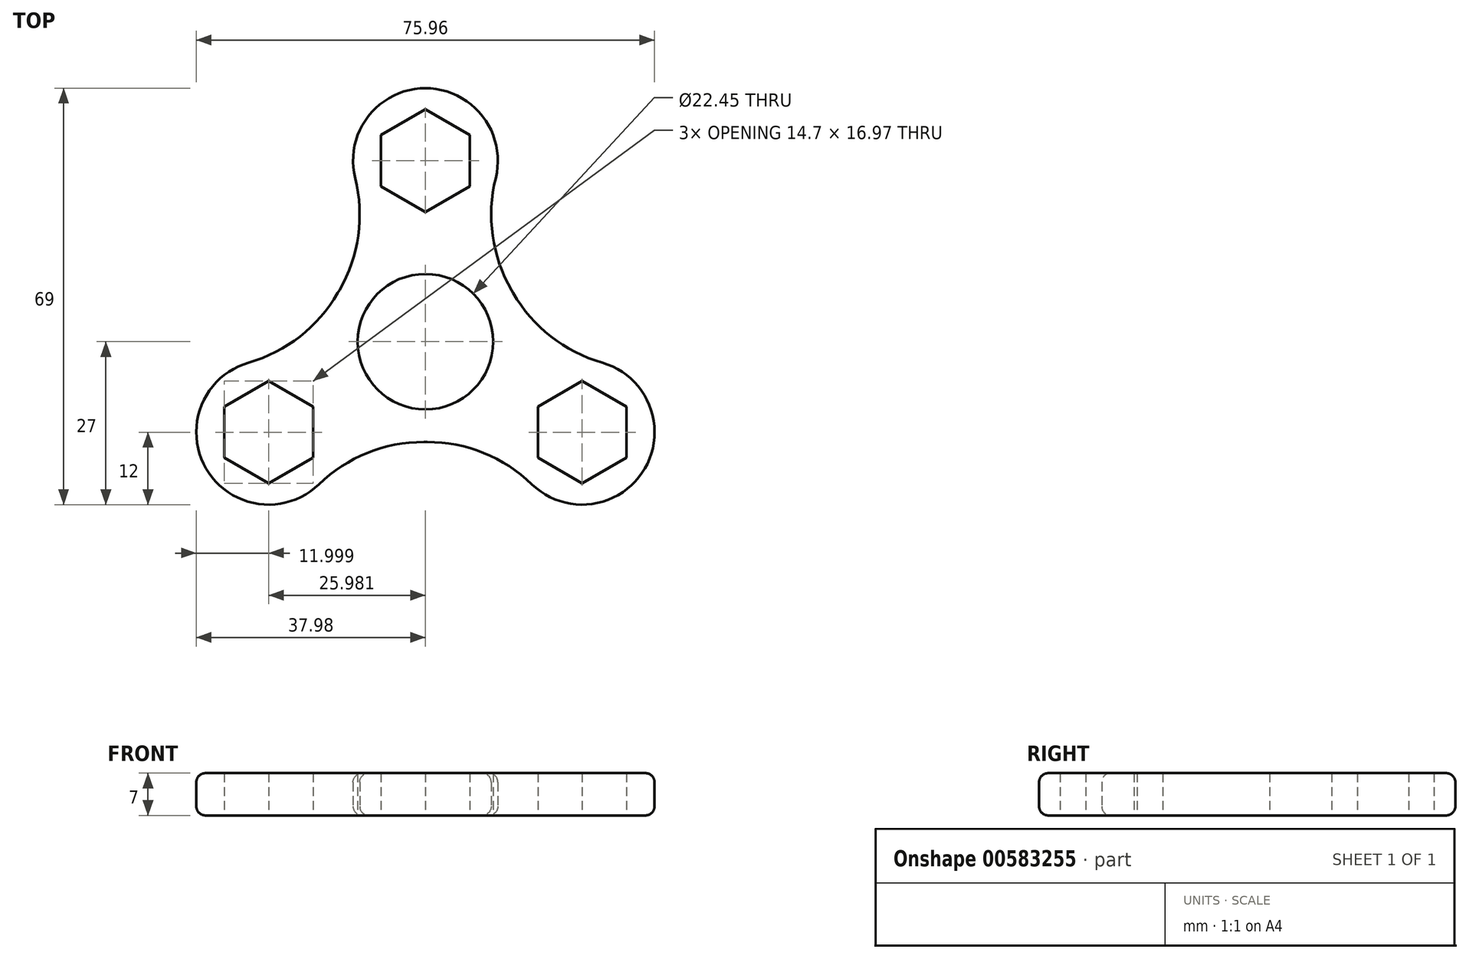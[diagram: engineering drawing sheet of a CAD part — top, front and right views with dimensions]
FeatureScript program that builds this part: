
annotation { "Feature Type Name" : "Feature", "Feature Type Description" : "" }
export const myFeature = defineFeature(function(context is Context, id is Id, definition is map)
    precondition{}
    {
        {
            var Q0;
            Q0=qCreatedBy(makeId("Top.planeOp"),FACE);
            var sketch = newSketch(context, id + "F0", { "sketchPlane" : qUnion([Q0])});
            skCircle(sketch, "E0", {"center": v(0, 0) * mm, "radius": 11.23 * mm});
            skCircle(sketch, "E1.cCircle", {"center": v(0, 30) * mm, "radius": 7.35 * mm, "construction": true});
            skLineSegment(sketch, "E1.0", {"start": v(7.35, 34.24) * mm, "end": v(7.35, 25.76) * mm});
            skLineSegment(sketch, "E1.1", {"start": v(7.35, 25.76) * mm, "end": v(0, 21.51) * mm});
            skLineSegment(sketch, "E1.2", {"start": v(0, 21.51) * mm, "end": v(-7.35, 25.76) * mm});
            skLineSegment(sketch, "E1.3", {"start": v(-7.35, 25.76) * mm, "end": v(-7.35, 34.24) * mm});
            skLineSegment(sketch, "E1.4", {"start": v(-7.35, 34.24) * mm, "end": v(0, 38.49) * mm});
            skLineSegment(sketch, "E1.5", {"start": v(0, 38.49) * mm, "end": v(7.35, 34.24) * mm});
            skPoint(sketch, "E1.0.midPoint", {"position": v(7.35, 30) * mm});
            skPoint(sketch, "E2.1.0", {"position": v(-29.66, -8.63) * mm});
            skLineSegment(sketch, "E2.1.1", {"start": v(-33.33, -19.24) * mm, "end": v(-33.33, -10.76) * mm});
            skLineSegment(sketch, "E2.1.2", {"start": v(-25.98, -23.49) * mm, "end": v(-33.33, -19.24) * mm});
            skLineSegment(sketch, "E2.1.3", {"start": v(-18.63, -19.24) * mm, "end": v(-25.98, -23.49) * mm});
            skLineSegment(sketch, "E2.1.4", {"start": v(-18.63, -10.76) * mm, "end": v(-18.63, -19.24) * mm});
            skLineSegment(sketch, "E2.1.5", {"start": v(-25.98, -6.51) * mm, "end": v(-18.63, -10.76) * mm});
            skLineSegment(sketch, "E2.1.6", {"start": v(-33.33, -10.76) * mm, "end": v(-25.98, -6.51) * mm});
            skCircle(sketch, "E2.1.7", {"center": v(-25.98, -15) * mm, "radius": 7.35 * mm, "construction": true});
            skPoint(sketch, "E2.2.0", {"position": v(22.3, -21.37) * mm});
            skLineSegment(sketch, "E2.2.1", {"start": v(33.33, -19.24) * mm, "end": v(25.98, -23.49) * mm});
            skLineSegment(sketch, "E2.2.2", {"start": v(33.33, -10.76) * mm, "end": v(33.33, -19.24) * mm});
            skLineSegment(sketch, "E2.2.3", {"start": v(25.98, -6.51) * mm, "end": v(33.33, -10.76) * mm});
            skLineSegment(sketch, "E2.2.4", {"start": v(18.63, -10.76) * mm, "end": v(25.98, -6.51) * mm});
            skLineSegment(sketch, "E2.2.5", {"start": v(18.63, -19.24) * mm, "end": v(18.63, -10.76) * mm});
            skLineSegment(sketch, "E2.2.6", {"start": v(25.98, -23.49) * mm, "end": v(18.63, -19.24) * mm});
            skCircle(sketch, "E2.2.7", {"center": v(25.98, -15) * mm, "radius": 7.35 * mm, "construction": true});
            skArc(sketch, "E3.0", {"start": v(-8.85, -13.6) * mm, "mid": v(0, -16.23) * mm, "end": v(8.85, -13.6) * mm});
            skArc(sketch, "E4", {"start": v(-21.44, -3.9) * mm, "mid": v(-36.37, -21) * mm, "end": v(-14.1, -16.62) * mm});
            skArc(sketch, "E5", {"start": v(7.35, 20.51) * mm, "mid": v(0, 42) * mm, "end": v(-7.35, 20.51) * mm});
            skArc(sketch, "E6", {"start": v(14.1, -16.62) * mm, "mid": v(36.37, -21) * mm, "end": v(21.44, -3.9) * mm});
            skLineSegment(sketch, "E7", {"start": v(-14.1, -16.62) * mm, "end": v(-8.85, -13.6) * mm});
            skLineSegment(sketch, "E8", {"start": v(-21.44, -3.9) * mm, "end": v(-16.2, -0.87) * mm});
            skLineSegment(sketch, "E9.1.0", {"start": v(14.1, -16.62) * mm, "end": v(8.85, -13.6) * mm});
            skLineSegment(sketch, "E9.1.1", {"start": v(21.44, -3.9) * mm, "end": v(16.2, -0.87) * mm});
            skLineSegment(sketch, "E9.2.0", {"start": v(7.35, 20.51) * mm, "end": v(7.35, 14.46) * mm});
            skLineSegment(sketch, "E9.2.1", {"start": v(-7.35, 20.51) * mm, "end": v(-7.35, 14.46) * mm});
            skArc(sketch, "E10.trimOffspring", {"start": v(16.2, -0.87) * mm, "mid": v(14.05, 8.11) * mm, "end": v(7.35, 14.46) * mm});
            skArc(sketch, "E11.trimOffspring", {"start": v(-7.35, 14.46) * mm, "mid": v(-14.05, 8.11) * mm, "end": v(-16.2, -0.87) * mm});
            skLineSegment(sketch, "E12", {"start": v(-7.35, 20.51) * mm, "end": v(-21.44, -3.9) * mm});
            skLineSegment(sketch, "E13", {"start": v(7.35, 20.51) * mm, "end": v(21.44, -3.9) * mm});
            skLineSegment(sketch, "E14", {"start": v(14.1, -16.62) * mm, "end": v(-14.1, -16.62) * mm});
            skSolve(sketch);
        }
        {
            var Q0;
            Q0=makeQuery(id+"F0.imprint","IMPRINT",FACE,{"disambiguationData":[TD([[makeQuery(id+"F0.imprint","IMPRINT",EDGE,{"derivedFrom":sQuery(id+"F0.wireOp",EDGE,"E0")}),-1.0]])]});
            var Q1;
            {var subQ0=sQuery(id+"F0.wireOp",EDGE,"E9.2.1");Q1=makeQuery(id+"F0.imprint","IMPRINT",FACE,{"disambiguationData":[TD([[makeQuery(id+"F0.imprint","IMPRINT",EDGE,{"derivedFrom":subQ0}),-1.0]])]});}
            var Q2;
            {var subQ0=sQuery(id+"F0.wireOp",EDGE,"E9.1.1");Q2=makeQuery(id+"F0.imprint","IMPRINT",FACE,{"disambiguationData":[TD([[makeQuery(id+"F0.imprint","IMPRINT",EDGE,{"derivedFrom":subQ0}),-1.0]])]});}
            var Q3;
            {var subQ0=sQuery(id+"F0.wireOp",EDGE,"E7");Q3=makeQuery(id+"F0.imprint","IMPRINT",FACE,{"disambiguationData":[TD([[makeQuery(id+"F0.imprint","IMPRINT",EDGE,{"derivedFrom":subQ0}),-1.0]])]});}
            extrude(context, id + "F1", {"entities" : qUnion([Q0, Q1, Q2, Q3]), "depth" : 7 * mm, "offsetDistance" : 25 * mm});
        }
        {
            var Q0;
            Q0=makeQuery(id+"F1.opExtrude","SWEPT_EDGE",EDGE,{"disambiguationData":[OSD([sQuery(id+"F0.wireOp",EDGE,"E4"),sQuery(id+"F0.wireOp",EDGE,"E8")])]});
            var Q1;
            Q1=makeQuery(id+"F1.opExtrude","SWEPT_EDGE",EDGE,{"disambiguationData":[OSD([sQuery(id+"F0.wireOp",EDGE,"E8"),sQuery(id+"F0.wireOp",EDGE,"E11.trimOffspring")])]});
            var Q2;
            Q2=makeQuery(id+"F1.opExtrude","SWEPT_EDGE",EDGE,{"disambiguationData":[OSD([sQuery(id+"F0.wireOp",EDGE,"E5"),sQuery(id+"F0.wireOp",EDGE,"fxcDau1n-MOiw-X37I-9tvh-2hMDEvbzTq9I")])]});
            var Q3;
            Q3=makeQuery(id+"F1.opExtrude","SWEPT_EDGE",EDGE,{"disambiguationData":[OSD([sQuery(id+"F0.wireOp",EDGE,"E9.2.0"),sQuery(id+"F0.wireOp",EDGE,"E10.trimOffspring")])]});
            var Q4;
            Q4=makeQuery(id+"F1.opExtrude","SWEPT_EDGE",EDGE,{"disambiguationData":[OSD([sQuery(id+"F0.wireOp",EDGE,"E5"),sQuery(id+"F0.wireOp",EDGE,"E9.2.0")])]});
            var Q5;
            Q5=makeQuery(id+"F1.opExtrude","SWEPT_EDGE",EDGE,{"disambiguationData":[OSD([sQuery(id+"F0.wireOp",EDGE,"E3.0"),sQuery(id+"F0.wireOp",EDGE,"E9.1.0")])]});
            var Q6;
            Q6=makeQuery(id+"F1.opExtrude","SWEPT_EDGE",EDGE,{"disambiguationData":[OSD([sQuery(id+"F0.wireOp",EDGE,"E6"),sQuery(id+"F0.wireOp",EDGE,"E9.1.0")])]});
            var Q7;
            Q7=makeQuery(id+"F1.opExtrude","SWEPT_EDGE",EDGE,{"disambiguationData":[OSD([sQuery(id+"F0.wireOp",EDGE,"E6"),sQuery(id+"F0.wireOp",EDGE,"90fa9932-7e28-47d2-bc1e-430a4b0f63f5.2.0")])]});
            var Q8;
            Q8=makeQuery(id+"F1.opExtrude","SWEPT_EDGE",EDGE,{"disambiguationData":[OSD([sQuery(id+"F0.wireOp",EDGE,"E4"),sQuery(id+"F0.wireOp",EDGE,"90fa9932-7e28-47d2-bc1e-430a4b0f63f5.1.0")])]});
            fillet(context, id + "F2", {"entities" : qUnion([Q0, Q1, Q2, Q3, Q4, Q5, Q6, Q7, Q8]), "radius" : 25 * mm, "tangentPropagation" : true, "allowEdgeOverflow" : false});
        }
        {
            var Q0;
            {var subQ0=sQuery(id+"F0.wireOp",EDGE,"E11.trimOffspring");var subQ1=sQuery(id+"F0.wireOp",EDGE,"E9.2.1");Q0=makeQuery(id+"F2.opFillet","BLEND_EDGE",EDGE,{"blendedFrom":[makeQuery(id+"F1.opExtrude","SWEPT_EDGE",EDGE,{"disambiguationData":[OSD([subQ1,subQ0])]}),makeQuery(id+"F1.opExtrude","CAP_FACE",FACE,{"disambiguationData":[OSD([sQuery(id+"F0.wireOp",EDGE,"E0"),sQuery(id+"F0.wireOp",EDGE,"E1.0"),sQuery(id+"F0.wireOp",EDGE,"E1.1"),sQuery(id+"F0.wireOp",EDGE,"E1.2"),sQuery(id+"F0.wireOp",EDGE,"E1.3"),sQuery(id+"F0.wireOp",EDGE,"E1.4"),sQuery(id+"F0.wireOp",EDGE,"E1.5"),sQuery(id+"F0.wireOp",EDGE,"E2.1.1"),sQuery(id+"F0.wireOp",EDGE,"E2.1.2"),sQuery(id+"F0.wireOp",EDGE,"E2.1.3"),sQuery(id+"F0.wireOp",EDGE,"E2.1.4"),sQuery(id+"F0.wireOp",EDGE,"E2.1.5"),sQuery(id+"F0.wireOp",EDGE,"E2.1.6"),sQuery(id+"F0.wireOp",EDGE,"E2.2.1"),sQuery(id+"F0.wireOp",EDGE,"E2.2.2"),sQuery(id+"F0.wireOp",EDGE,"E2.2.3"),sQuery(id+"F0.wireOp",EDGE,"E2.2.4"),sQuery(id+"F0.wireOp",EDGE,"E2.2.5"),sQuery(id+"F0.wireOp",EDGE,"E2.2.6"),sQuery(id+"F0.wireOp",EDGE,"E3.0"),sQuery(id+"F0.wireOp",EDGE,"E4"),sQuery(id+"F0.wireOp",EDGE,"E5"),sQuery(id+"F0.wireOp",EDGE,"E6"),sQuery(id+"F0.wireOp",EDGE,"E7"),sQuery(id+"F0.wireOp",EDGE,"E8"),sQuery(id+"F0.wireOp",EDGE,"E9.1.0"),sQuery(id+"F0.wireOp",EDGE,"E9.1.1"),sQuery(id+"F0.wireOp",EDGE,"E9.2.0"),subQ1,sQuery(id+"F0.wireOp",EDGE,"E10.trimOffspring"),subQ0])],"isStart":false})],"blendedInto":[makeQuery(id+"F1.opExtrude","CAP_FACE",FACE,{"disambiguationData":[OSD([sQuery(id+"F0.wireOp",EDGE,"E0"),sQuery(id+"F0.wireOp",EDGE,"E1.0"),sQuery(id+"F0.wireOp",EDGE,"E1.1"),sQuery(id+"F0.wireOp",EDGE,"E1.2"),sQuery(id+"F0.wireOp",EDGE,"E1.3"),sQuery(id+"F0.wireOp",EDGE,"E1.4"),sQuery(id+"F0.wireOp",EDGE,"E1.5"),sQuery(id+"F0.wireOp",EDGE,"E2.1.1"),sQuery(id+"F0.wireOp",EDGE,"E2.1.2"),sQuery(id+"F0.wireOp",EDGE,"E2.1.3"),sQuery(id+"F0.wireOp",EDGE,"E2.1.4"),sQuery(id+"F0.wireOp",EDGE,"E2.1.5"),sQuery(id+"F0.wireOp",EDGE,"E2.1.6"),sQuery(id+"F0.wireOp",EDGE,"E2.2.1"),sQuery(id+"F0.wireOp",EDGE,"E2.2.2"),sQuery(id+"F0.wireOp",EDGE,"E2.2.3"),sQuery(id+"F0.wireOp",EDGE,"E2.2.4"),sQuery(id+"F0.wireOp",EDGE,"E2.2.5"),sQuery(id+"F0.wireOp",EDGE,"E2.2.6"),sQuery(id+"F0.wireOp",EDGE,"E3.0"),sQuery(id+"F0.wireOp",EDGE,"E4"),sQuery(id+"F0.wireOp",EDGE,"E5"),sQuery(id+"F0.wireOp",EDGE,"E6"),sQuery(id+"F0.wireOp",EDGE,"E7"),sQuery(id+"F0.wireOp",EDGE,"E8"),sQuery(id+"F0.wireOp",EDGE,"E9.1.0"),sQuery(id+"F0.wireOp",EDGE,"E9.1.1"),sQuery(id+"F0.wireOp",EDGE,"E9.2.0"),subQ1,sQuery(id+"F0.wireOp",EDGE,"E10.trimOffspring"),subQ0])],"isStart":false})]});}
            var Q1;
            Q1=makeQuery(id+"F1.opExtrude","CAP_EDGE",EDGE,{"disambiguationData":[OSD([sQuery(id+"F0.wireOp",EDGE,"E11.trimOffspring")])],"isStart":false});
            var Q2;
            {var subQ0=sQuery(id+"F0.wireOp",EDGE,"E8");var subQ1=sQuery(id+"F0.wireOp",EDGE,"E4");Q2=makeQuery(id+"F2.opFillet","BLEND_EDGE",EDGE,{"blendedFrom":[makeQuery(id+"F1.opExtrude","SWEPT_EDGE",EDGE,{"disambiguationData":[OSD([subQ1,subQ0])]}),makeQuery(id+"F1.opExtrude","CAP_FACE",FACE,{"disambiguationData":[OSD([sQuery(id+"F0.wireOp",EDGE,"E0"),sQuery(id+"F0.wireOp",EDGE,"E1.0"),sQuery(id+"F0.wireOp",EDGE,"E1.1"),sQuery(id+"F0.wireOp",EDGE,"E1.2"),sQuery(id+"F0.wireOp",EDGE,"E1.3"),sQuery(id+"F0.wireOp",EDGE,"E1.4"),sQuery(id+"F0.wireOp",EDGE,"E1.5"),sQuery(id+"F0.wireOp",EDGE,"E2.1.1"),sQuery(id+"F0.wireOp",EDGE,"E2.1.2"),sQuery(id+"F0.wireOp",EDGE,"E2.1.3"),sQuery(id+"F0.wireOp",EDGE,"E2.1.4"),sQuery(id+"F0.wireOp",EDGE,"E2.1.5"),sQuery(id+"F0.wireOp",EDGE,"E2.1.6"),sQuery(id+"F0.wireOp",EDGE,"E2.2.1"),sQuery(id+"F0.wireOp",EDGE,"E2.2.2"),sQuery(id+"F0.wireOp",EDGE,"E2.2.3"),sQuery(id+"F0.wireOp",EDGE,"E2.2.4"),sQuery(id+"F0.wireOp",EDGE,"E2.2.5"),sQuery(id+"F0.wireOp",EDGE,"E2.2.6"),sQuery(id+"F0.wireOp",EDGE,"E3.0"),subQ1,sQuery(id+"F0.wireOp",EDGE,"E5"),sQuery(id+"F0.wireOp",EDGE,"E6"),sQuery(id+"F0.wireOp",EDGE,"E7"),subQ0,sQuery(id+"F0.wireOp",EDGE,"E9.1.0"),sQuery(id+"F0.wireOp",EDGE,"E9.1.1"),sQuery(id+"F0.wireOp",EDGE,"E9.2.0"),sQuery(id+"F0.wireOp",EDGE,"E9.2.1"),sQuery(id+"F0.wireOp",EDGE,"E10.trimOffspring"),sQuery(id+"F0.wireOp",EDGE,"E11.trimOffspring")])],"isStart":false})],"blendedInto":[makeQuery(id+"F1.opExtrude","CAP_FACE",FACE,{"disambiguationData":[OSD([sQuery(id+"F0.wireOp",EDGE,"E0"),sQuery(id+"F0.wireOp",EDGE,"E1.0"),sQuery(id+"F0.wireOp",EDGE,"E1.1"),sQuery(id+"F0.wireOp",EDGE,"E1.2"),sQuery(id+"F0.wireOp",EDGE,"E1.3"),sQuery(id+"F0.wireOp",EDGE,"E1.4"),sQuery(id+"F0.wireOp",EDGE,"E1.5"),sQuery(id+"F0.wireOp",EDGE,"E2.1.1"),sQuery(id+"F0.wireOp",EDGE,"E2.1.2"),sQuery(id+"F0.wireOp",EDGE,"E2.1.3"),sQuery(id+"F0.wireOp",EDGE,"E2.1.4"),sQuery(id+"F0.wireOp",EDGE,"E2.1.5"),sQuery(id+"F0.wireOp",EDGE,"E2.1.6"),sQuery(id+"F0.wireOp",EDGE,"E2.2.1"),sQuery(id+"F0.wireOp",EDGE,"E2.2.2"),sQuery(id+"F0.wireOp",EDGE,"E2.2.3"),sQuery(id+"F0.wireOp",EDGE,"E2.2.4"),sQuery(id+"F0.wireOp",EDGE,"E2.2.5"),sQuery(id+"F0.wireOp",EDGE,"E2.2.6"),sQuery(id+"F0.wireOp",EDGE,"E3.0"),subQ1,sQuery(id+"F0.wireOp",EDGE,"E5"),sQuery(id+"F0.wireOp",EDGE,"E6"),sQuery(id+"F0.wireOp",EDGE,"E7"),subQ0,sQuery(id+"F0.wireOp",EDGE,"E9.1.0"),sQuery(id+"F0.wireOp",EDGE,"E9.1.1"),sQuery(id+"F0.wireOp",EDGE,"E9.2.0"),sQuery(id+"F0.wireOp",EDGE,"E9.2.1"),sQuery(id+"F0.wireOp",EDGE,"E10.trimOffspring"),sQuery(id+"F0.wireOp",EDGE,"E11.trimOffspring")])],"isStart":false})]});}
            var Q3;
            Q3=makeQuery(id+"F1.opExtrude","CAP_EDGE",EDGE,{"disambiguationData":[OSD([sQuery(id+"F0.wireOp",EDGE,"E4")])],"isStart":false});
            var Q4;
            {var subQ0=sQuery(id+"F0.wireOp",EDGE,"E7");var subQ1=sQuery(id+"F0.wireOp",EDGE,"E3.0");Q4=makeQuery(id+"F2.opFillet","BLEND_EDGE",EDGE,{"blendedFrom":[makeQuery(id+"F1.opExtrude","SWEPT_EDGE",EDGE,{"disambiguationData":[OSD([subQ1,subQ0])]}),makeQuery(id+"F1.opExtrude","CAP_FACE",FACE,{"disambiguationData":[OSD([sQuery(id+"F0.wireOp",EDGE,"E0"),sQuery(id+"F0.wireOp",EDGE,"E1.0"),sQuery(id+"F0.wireOp",EDGE,"E1.1"),sQuery(id+"F0.wireOp",EDGE,"E1.2"),sQuery(id+"F0.wireOp",EDGE,"E1.3"),sQuery(id+"F0.wireOp",EDGE,"E1.4"),sQuery(id+"F0.wireOp",EDGE,"E1.5"),sQuery(id+"F0.wireOp",EDGE,"E2.1.1"),sQuery(id+"F0.wireOp",EDGE,"E2.1.2"),sQuery(id+"F0.wireOp",EDGE,"E2.1.3"),sQuery(id+"F0.wireOp",EDGE,"E2.1.4"),sQuery(id+"F0.wireOp",EDGE,"E2.1.5"),sQuery(id+"F0.wireOp",EDGE,"E2.1.6"),sQuery(id+"F0.wireOp",EDGE,"E2.2.1"),sQuery(id+"F0.wireOp",EDGE,"E2.2.2"),sQuery(id+"F0.wireOp",EDGE,"E2.2.3"),sQuery(id+"F0.wireOp",EDGE,"E2.2.4"),sQuery(id+"F0.wireOp",EDGE,"E2.2.5"),sQuery(id+"F0.wireOp",EDGE,"E2.2.6"),subQ1,sQuery(id+"F0.wireOp",EDGE,"E4"),sQuery(id+"F0.wireOp",EDGE,"E5"),sQuery(id+"F0.wireOp",EDGE,"E6"),subQ0,sQuery(id+"F0.wireOp",EDGE,"E8"),sQuery(id+"F0.wireOp",EDGE,"E9.1.0"),sQuery(id+"F0.wireOp",EDGE,"E9.1.1"),sQuery(id+"F0.wireOp",EDGE,"E9.2.0"),sQuery(id+"F0.wireOp",EDGE,"E9.2.1"),sQuery(id+"F0.wireOp",EDGE,"E10.trimOffspring"),sQuery(id+"F0.wireOp",EDGE,"E11.trimOffspring")])],"isStart":false})],"blendedInto":[makeQuery(id+"F1.opExtrude","CAP_FACE",FACE,{"disambiguationData":[OSD([sQuery(id+"F0.wireOp",EDGE,"E0"),sQuery(id+"F0.wireOp",EDGE,"E1.0"),sQuery(id+"F0.wireOp",EDGE,"E1.1"),sQuery(id+"F0.wireOp",EDGE,"E1.2"),sQuery(id+"F0.wireOp",EDGE,"E1.3"),sQuery(id+"F0.wireOp",EDGE,"E1.4"),sQuery(id+"F0.wireOp",EDGE,"E1.5"),sQuery(id+"F0.wireOp",EDGE,"E2.1.1"),sQuery(id+"F0.wireOp",EDGE,"E2.1.2"),sQuery(id+"F0.wireOp",EDGE,"E2.1.3"),sQuery(id+"F0.wireOp",EDGE,"E2.1.4"),sQuery(id+"F0.wireOp",EDGE,"E2.1.5"),sQuery(id+"F0.wireOp",EDGE,"E2.1.6"),sQuery(id+"F0.wireOp",EDGE,"E2.2.1"),sQuery(id+"F0.wireOp",EDGE,"E2.2.2"),sQuery(id+"F0.wireOp",EDGE,"E2.2.3"),sQuery(id+"F0.wireOp",EDGE,"E2.2.4"),sQuery(id+"F0.wireOp",EDGE,"E2.2.5"),sQuery(id+"F0.wireOp",EDGE,"E2.2.6"),subQ1,sQuery(id+"F0.wireOp",EDGE,"E4"),sQuery(id+"F0.wireOp",EDGE,"E5"),sQuery(id+"F0.wireOp",EDGE,"E6"),subQ0,sQuery(id+"F0.wireOp",EDGE,"E8"),sQuery(id+"F0.wireOp",EDGE,"E9.1.0"),sQuery(id+"F0.wireOp",EDGE,"E9.1.1"),sQuery(id+"F0.wireOp",EDGE,"E9.2.0"),sQuery(id+"F0.wireOp",EDGE,"E9.2.1"),sQuery(id+"F0.wireOp",EDGE,"E10.trimOffspring"),sQuery(id+"F0.wireOp",EDGE,"E11.trimOffspring")])],"isStart":false})]});}
            var Q5;
            Q5=makeQuery(id+"F1.opExtrude","CAP_EDGE",EDGE,{"disambiguationData":[OSD([sQuery(id+"F0.wireOp",EDGE,"E6")])],"isStart":false});
            var Q6;
            {var subQ0=sQuery(id+"F0.wireOp",EDGE,"E10.trimOffspring");var subQ1=sQuery(id+"F0.wireOp",EDGE,"E9.1.1");Q6=makeQuery(id+"F2.opFillet","BLEND_EDGE",EDGE,{"blendedFrom":[makeQuery(id+"F1.opExtrude","SWEPT_EDGE",EDGE,{"disambiguationData":[OSD([subQ1,subQ0])]}),makeQuery(id+"F1.opExtrude","CAP_FACE",FACE,{"disambiguationData":[OSD([sQuery(id+"F0.wireOp",EDGE,"E0"),sQuery(id+"F0.wireOp",EDGE,"E1.0"),sQuery(id+"F0.wireOp",EDGE,"E1.1"),sQuery(id+"F0.wireOp",EDGE,"E1.2"),sQuery(id+"F0.wireOp",EDGE,"E1.3"),sQuery(id+"F0.wireOp",EDGE,"E1.4"),sQuery(id+"F0.wireOp",EDGE,"E1.5"),sQuery(id+"F0.wireOp",EDGE,"E2.1.1"),sQuery(id+"F0.wireOp",EDGE,"E2.1.2"),sQuery(id+"F0.wireOp",EDGE,"E2.1.3"),sQuery(id+"F0.wireOp",EDGE,"E2.1.4"),sQuery(id+"F0.wireOp",EDGE,"E2.1.5"),sQuery(id+"F0.wireOp",EDGE,"E2.1.6"),sQuery(id+"F0.wireOp",EDGE,"E2.2.1"),sQuery(id+"F0.wireOp",EDGE,"E2.2.2"),sQuery(id+"F0.wireOp",EDGE,"E2.2.3"),sQuery(id+"F0.wireOp",EDGE,"E2.2.4"),sQuery(id+"F0.wireOp",EDGE,"E2.2.5"),sQuery(id+"F0.wireOp",EDGE,"E2.2.6"),sQuery(id+"F0.wireOp",EDGE,"E3.0"),sQuery(id+"F0.wireOp",EDGE,"E4"),sQuery(id+"F0.wireOp",EDGE,"E5"),sQuery(id+"F0.wireOp",EDGE,"E6"),sQuery(id+"F0.wireOp",EDGE,"E7"),sQuery(id+"F0.wireOp",EDGE,"E8"),sQuery(id+"F0.wireOp",EDGE,"E9.1.0"),subQ1,sQuery(id+"F0.wireOp",EDGE,"E9.2.0"),sQuery(id+"F0.wireOp",EDGE,"E9.2.1"),subQ0,sQuery(id+"F0.wireOp",EDGE,"E11.trimOffspring")])],"isStart":false})],"blendedInto":[makeQuery(id+"F1.opExtrude","CAP_FACE",FACE,{"disambiguationData":[OSD([sQuery(id+"F0.wireOp",EDGE,"E0"),sQuery(id+"F0.wireOp",EDGE,"E1.0"),sQuery(id+"F0.wireOp",EDGE,"E1.1"),sQuery(id+"F0.wireOp",EDGE,"E1.2"),sQuery(id+"F0.wireOp",EDGE,"E1.3"),sQuery(id+"F0.wireOp",EDGE,"E1.4"),sQuery(id+"F0.wireOp",EDGE,"E1.5"),sQuery(id+"F0.wireOp",EDGE,"E2.1.1"),sQuery(id+"F0.wireOp",EDGE,"E2.1.2"),sQuery(id+"F0.wireOp",EDGE,"E2.1.3"),sQuery(id+"F0.wireOp",EDGE,"E2.1.4"),sQuery(id+"F0.wireOp",EDGE,"E2.1.5"),sQuery(id+"F0.wireOp",EDGE,"E2.1.6"),sQuery(id+"F0.wireOp",EDGE,"E2.2.1"),sQuery(id+"F0.wireOp",EDGE,"E2.2.2"),sQuery(id+"F0.wireOp",EDGE,"E2.2.3"),sQuery(id+"F0.wireOp",EDGE,"E2.2.4"),sQuery(id+"F0.wireOp",EDGE,"E2.2.5"),sQuery(id+"F0.wireOp",EDGE,"E2.2.6"),sQuery(id+"F0.wireOp",EDGE,"E3.0"),sQuery(id+"F0.wireOp",EDGE,"E4"),sQuery(id+"F0.wireOp",EDGE,"E5"),sQuery(id+"F0.wireOp",EDGE,"E6"),sQuery(id+"F0.wireOp",EDGE,"E7"),sQuery(id+"F0.wireOp",EDGE,"E8"),sQuery(id+"F0.wireOp",EDGE,"E9.1.0"),subQ1,sQuery(id+"F0.wireOp",EDGE,"E9.2.0"),sQuery(id+"F0.wireOp",EDGE,"E9.2.1"),subQ0,sQuery(id+"F0.wireOp",EDGE,"E11.trimOffspring")])],"isStart":false})]});}
            var Q7;
            {var subQ0=sQuery(id+"F0.wireOp",EDGE,"E10.trimOffspring");var subQ1=sQuery(id+"F0.wireOp",EDGE,"E9.2.0");Q7=makeQuery(id+"F2.opFillet","BLEND_EDGE",EDGE,{"blendedFrom":[makeQuery(id+"F1.opExtrude","SWEPT_EDGE",EDGE,{"disambiguationData":[OSD([subQ1,subQ0])]}),makeQuery(id+"F1.opExtrude","CAP_FACE",FACE,{"disambiguationData":[OSD([sQuery(id+"F0.wireOp",EDGE,"E0"),sQuery(id+"F0.wireOp",EDGE,"E1.0"),sQuery(id+"F0.wireOp",EDGE,"E1.1"),sQuery(id+"F0.wireOp",EDGE,"E1.2"),sQuery(id+"F0.wireOp",EDGE,"E1.3"),sQuery(id+"F0.wireOp",EDGE,"E1.4"),sQuery(id+"F0.wireOp",EDGE,"E1.5"),sQuery(id+"F0.wireOp",EDGE,"E2.1.1"),sQuery(id+"F0.wireOp",EDGE,"E2.1.2"),sQuery(id+"F0.wireOp",EDGE,"E2.1.3"),sQuery(id+"F0.wireOp",EDGE,"E2.1.4"),sQuery(id+"F0.wireOp",EDGE,"E2.1.5"),sQuery(id+"F0.wireOp",EDGE,"E2.1.6"),sQuery(id+"F0.wireOp",EDGE,"E2.2.1"),sQuery(id+"F0.wireOp",EDGE,"E2.2.2"),sQuery(id+"F0.wireOp",EDGE,"E2.2.3"),sQuery(id+"F0.wireOp",EDGE,"E2.2.4"),sQuery(id+"F0.wireOp",EDGE,"E2.2.5"),sQuery(id+"F0.wireOp",EDGE,"E2.2.6"),sQuery(id+"F0.wireOp",EDGE,"E3.0"),sQuery(id+"F0.wireOp",EDGE,"E4"),sQuery(id+"F0.wireOp",EDGE,"E5"),sQuery(id+"F0.wireOp",EDGE,"E6"),sQuery(id+"F0.wireOp",EDGE,"E7"),sQuery(id+"F0.wireOp",EDGE,"E8"),sQuery(id+"F0.wireOp",EDGE,"E9.1.0"),sQuery(id+"F0.wireOp",EDGE,"E9.1.1"),subQ1,sQuery(id+"F0.wireOp",EDGE,"E9.2.1"),subQ0,sQuery(id+"F0.wireOp",EDGE,"E11.trimOffspring")])],"isStart":false})],"blendedInto":[makeQuery(id+"F1.opExtrude","CAP_FACE",FACE,{"disambiguationData":[OSD([sQuery(id+"F0.wireOp",EDGE,"E0"),sQuery(id+"F0.wireOp",EDGE,"E1.0"),sQuery(id+"F0.wireOp",EDGE,"E1.1"),sQuery(id+"F0.wireOp",EDGE,"E1.2"),sQuery(id+"F0.wireOp",EDGE,"E1.3"),sQuery(id+"F0.wireOp",EDGE,"E1.4"),sQuery(id+"F0.wireOp",EDGE,"E1.5"),sQuery(id+"F0.wireOp",EDGE,"E2.1.1"),sQuery(id+"F0.wireOp",EDGE,"E2.1.2"),sQuery(id+"F0.wireOp",EDGE,"E2.1.3"),sQuery(id+"F0.wireOp",EDGE,"E2.1.4"),sQuery(id+"F0.wireOp",EDGE,"E2.1.5"),sQuery(id+"F0.wireOp",EDGE,"E2.1.6"),sQuery(id+"F0.wireOp",EDGE,"E2.2.1"),sQuery(id+"F0.wireOp",EDGE,"E2.2.2"),sQuery(id+"F0.wireOp",EDGE,"E2.2.3"),sQuery(id+"F0.wireOp",EDGE,"E2.2.4"),sQuery(id+"F0.wireOp",EDGE,"E2.2.5"),sQuery(id+"F0.wireOp",EDGE,"E2.2.6"),sQuery(id+"F0.wireOp",EDGE,"E3.0"),sQuery(id+"F0.wireOp",EDGE,"E4"),sQuery(id+"F0.wireOp",EDGE,"E5"),sQuery(id+"F0.wireOp",EDGE,"E6"),sQuery(id+"F0.wireOp",EDGE,"E7"),sQuery(id+"F0.wireOp",EDGE,"E8"),sQuery(id+"F0.wireOp",EDGE,"E9.1.0"),sQuery(id+"F0.wireOp",EDGE,"E9.1.1"),subQ1,sQuery(id+"F0.wireOp",EDGE,"E9.2.1"),subQ0,sQuery(id+"F0.wireOp",EDGE,"E11.trimOffspring")])],"isStart":false})]});}
            var Q8;
            Q8=makeQuery(id+"F1.opExtrude","CAP_EDGE",EDGE,{"disambiguationData":[OSD([sQuery(id+"F0.wireOp",EDGE,"E5")])],"isStart":false});
            var Q9;
            Q9=makeQuery(id+"F1.opExtrude","CAP_EDGE",EDGE,{"disambiguationData":[OSD([sQuery(id+"F0.wireOp",EDGE,"E5")])],"isStart":true});
            var Q10;
            {var subQ0=sQuery(id+"F0.wireOp",EDGE,"E11.trimOffspring");var subQ1=sQuery(id+"F0.wireOp",EDGE,"E9.2.1");Q10=makeQuery(id+"F2.opFillet","BLEND_EDGE",EDGE,{"blendedFrom":[makeQuery(id+"F1.opExtrude","SWEPT_EDGE",EDGE,{"disambiguationData":[OSD([subQ1,subQ0])]}),makeQuery(id+"F1.opExtrude","CAP_FACE",FACE,{"disambiguationData":[OSD([sQuery(id+"F0.wireOp",EDGE,"E0"),sQuery(id+"F0.wireOp",EDGE,"E1.0"),sQuery(id+"F0.wireOp",EDGE,"E1.1"),sQuery(id+"F0.wireOp",EDGE,"E1.2"),sQuery(id+"F0.wireOp",EDGE,"E1.3"),sQuery(id+"F0.wireOp",EDGE,"E1.4"),sQuery(id+"F0.wireOp",EDGE,"E1.5"),sQuery(id+"F0.wireOp",EDGE,"E2.1.1"),sQuery(id+"F0.wireOp",EDGE,"E2.1.2"),sQuery(id+"F0.wireOp",EDGE,"E2.1.3"),sQuery(id+"F0.wireOp",EDGE,"E2.1.4"),sQuery(id+"F0.wireOp",EDGE,"E2.1.5"),sQuery(id+"F0.wireOp",EDGE,"E2.1.6"),sQuery(id+"F0.wireOp",EDGE,"E2.2.1"),sQuery(id+"F0.wireOp",EDGE,"E2.2.2"),sQuery(id+"F0.wireOp",EDGE,"E2.2.3"),sQuery(id+"F0.wireOp",EDGE,"E2.2.4"),sQuery(id+"F0.wireOp",EDGE,"E2.2.5"),sQuery(id+"F0.wireOp",EDGE,"E2.2.6"),sQuery(id+"F0.wireOp",EDGE,"E3.0"),sQuery(id+"F0.wireOp",EDGE,"E4"),sQuery(id+"F0.wireOp",EDGE,"E5"),sQuery(id+"F0.wireOp",EDGE,"E6"),sQuery(id+"F0.wireOp",EDGE,"E7"),sQuery(id+"F0.wireOp",EDGE,"E8"),sQuery(id+"F0.wireOp",EDGE,"E9.1.0"),sQuery(id+"F0.wireOp",EDGE,"E9.1.1"),sQuery(id+"F0.wireOp",EDGE,"E9.2.0"),subQ1,sQuery(id+"F0.wireOp",EDGE,"E10.trimOffspring"),subQ0])],"isStart":true})],"blendedInto":[makeQuery(id+"F1.opExtrude","CAP_FACE",FACE,{"disambiguationData":[OSD([sQuery(id+"F0.wireOp",EDGE,"E0"),sQuery(id+"F0.wireOp",EDGE,"E1.0"),sQuery(id+"F0.wireOp",EDGE,"E1.1"),sQuery(id+"F0.wireOp",EDGE,"E1.2"),sQuery(id+"F0.wireOp",EDGE,"E1.3"),sQuery(id+"F0.wireOp",EDGE,"E1.4"),sQuery(id+"F0.wireOp",EDGE,"E1.5"),sQuery(id+"F0.wireOp",EDGE,"E2.1.1"),sQuery(id+"F0.wireOp",EDGE,"E2.1.2"),sQuery(id+"F0.wireOp",EDGE,"E2.1.3"),sQuery(id+"F0.wireOp",EDGE,"E2.1.4"),sQuery(id+"F0.wireOp",EDGE,"E2.1.5"),sQuery(id+"F0.wireOp",EDGE,"E2.1.6"),sQuery(id+"F0.wireOp",EDGE,"E2.2.1"),sQuery(id+"F0.wireOp",EDGE,"E2.2.2"),sQuery(id+"F0.wireOp",EDGE,"E2.2.3"),sQuery(id+"F0.wireOp",EDGE,"E2.2.4"),sQuery(id+"F0.wireOp",EDGE,"E2.2.5"),sQuery(id+"F0.wireOp",EDGE,"E2.2.6"),sQuery(id+"F0.wireOp",EDGE,"E3.0"),sQuery(id+"F0.wireOp",EDGE,"E4"),sQuery(id+"F0.wireOp",EDGE,"E5"),sQuery(id+"F0.wireOp",EDGE,"E6"),sQuery(id+"F0.wireOp",EDGE,"E7"),sQuery(id+"F0.wireOp",EDGE,"E8"),sQuery(id+"F0.wireOp",EDGE,"E9.1.0"),sQuery(id+"F0.wireOp",EDGE,"E9.1.1"),sQuery(id+"F0.wireOp",EDGE,"E9.2.0"),subQ1,sQuery(id+"F0.wireOp",EDGE,"E10.trimOffspring"),subQ0])],"isStart":true})]});}
            var Q11;
            {var subQ0=sQuery(id+"F0.wireOp",EDGE,"E11.trimOffspring");var subQ1=sQuery(id+"F0.wireOp",EDGE,"E8");Q11=makeQuery(id+"F2.opFillet","BLEND_EDGE",EDGE,{"blendedFrom":[makeQuery(id+"F1.opExtrude","SWEPT_EDGE",EDGE,{"disambiguationData":[OSD([subQ1,subQ0])]}),makeQuery(id+"F1.opExtrude","CAP_FACE",FACE,{"disambiguationData":[OSD([sQuery(id+"F0.wireOp",EDGE,"E0"),sQuery(id+"F0.wireOp",EDGE,"E1.0"),sQuery(id+"F0.wireOp",EDGE,"E1.1"),sQuery(id+"F0.wireOp",EDGE,"E1.2"),sQuery(id+"F0.wireOp",EDGE,"E1.3"),sQuery(id+"F0.wireOp",EDGE,"E1.4"),sQuery(id+"F0.wireOp",EDGE,"E1.5"),sQuery(id+"F0.wireOp",EDGE,"E2.1.1"),sQuery(id+"F0.wireOp",EDGE,"E2.1.2"),sQuery(id+"F0.wireOp",EDGE,"E2.1.3"),sQuery(id+"F0.wireOp",EDGE,"E2.1.4"),sQuery(id+"F0.wireOp",EDGE,"E2.1.5"),sQuery(id+"F0.wireOp",EDGE,"E2.1.6"),sQuery(id+"F0.wireOp",EDGE,"E2.2.1"),sQuery(id+"F0.wireOp",EDGE,"E2.2.2"),sQuery(id+"F0.wireOp",EDGE,"E2.2.3"),sQuery(id+"F0.wireOp",EDGE,"E2.2.4"),sQuery(id+"F0.wireOp",EDGE,"E2.2.5"),sQuery(id+"F0.wireOp",EDGE,"E2.2.6"),sQuery(id+"F0.wireOp",EDGE,"E3.0"),sQuery(id+"F0.wireOp",EDGE,"E4"),sQuery(id+"F0.wireOp",EDGE,"E5"),sQuery(id+"F0.wireOp",EDGE,"E6"),sQuery(id+"F0.wireOp",EDGE,"E7"),subQ1,sQuery(id+"F0.wireOp",EDGE,"E9.1.0"),sQuery(id+"F0.wireOp",EDGE,"E9.1.1"),sQuery(id+"F0.wireOp",EDGE,"E9.2.0"),sQuery(id+"F0.wireOp",EDGE,"E9.2.1"),sQuery(id+"F0.wireOp",EDGE,"E10.trimOffspring"),subQ0])],"isStart":true})],"blendedInto":[makeQuery(id+"F1.opExtrude","CAP_FACE",FACE,{"disambiguationData":[OSD([sQuery(id+"F0.wireOp",EDGE,"E0"),sQuery(id+"F0.wireOp",EDGE,"E1.0"),sQuery(id+"F0.wireOp",EDGE,"E1.1"),sQuery(id+"F0.wireOp",EDGE,"E1.2"),sQuery(id+"F0.wireOp",EDGE,"E1.3"),sQuery(id+"F0.wireOp",EDGE,"E1.4"),sQuery(id+"F0.wireOp",EDGE,"E1.5"),sQuery(id+"F0.wireOp",EDGE,"E2.1.1"),sQuery(id+"F0.wireOp",EDGE,"E2.1.2"),sQuery(id+"F0.wireOp",EDGE,"E2.1.3"),sQuery(id+"F0.wireOp",EDGE,"E2.1.4"),sQuery(id+"F0.wireOp",EDGE,"E2.1.5"),sQuery(id+"F0.wireOp",EDGE,"E2.1.6"),sQuery(id+"F0.wireOp",EDGE,"E2.2.1"),sQuery(id+"F0.wireOp",EDGE,"E2.2.2"),sQuery(id+"F0.wireOp",EDGE,"E2.2.3"),sQuery(id+"F0.wireOp",EDGE,"E2.2.4"),sQuery(id+"F0.wireOp",EDGE,"E2.2.5"),sQuery(id+"F0.wireOp",EDGE,"E2.2.6"),sQuery(id+"F0.wireOp",EDGE,"E3.0"),sQuery(id+"F0.wireOp",EDGE,"E4"),sQuery(id+"F0.wireOp",EDGE,"E5"),sQuery(id+"F0.wireOp",EDGE,"E6"),sQuery(id+"F0.wireOp",EDGE,"E7"),subQ1,sQuery(id+"F0.wireOp",EDGE,"E9.1.0"),sQuery(id+"F0.wireOp",EDGE,"E9.1.1"),sQuery(id+"F0.wireOp",EDGE,"E9.2.0"),sQuery(id+"F0.wireOp",EDGE,"E9.2.1"),sQuery(id+"F0.wireOp",EDGE,"E10.trimOffspring"),subQ0])],"isStart":true})]});}
            var Q12;
            Q12=makeQuery(id+"F1.opExtrude","CAP_EDGE",EDGE,{"disambiguationData":[OSD([sQuery(id+"F0.wireOp",EDGE,"E4")])],"isStart":true});
            var Q13;
            {var subQ0=sQuery(id+"F0.wireOp",EDGE,"E7");var subQ1=sQuery(id+"F0.wireOp",EDGE,"E3.0");Q13=makeQuery(id+"F2.opFillet","BLEND_EDGE",EDGE,{"blendedFrom":[makeQuery(id+"F1.opExtrude","SWEPT_EDGE",EDGE,{"disambiguationData":[OSD([subQ1,subQ0])]}),makeQuery(id+"F1.opExtrude","CAP_FACE",FACE,{"disambiguationData":[OSD([sQuery(id+"F0.wireOp",EDGE,"E0"),sQuery(id+"F0.wireOp",EDGE,"E1.0"),sQuery(id+"F0.wireOp",EDGE,"E1.1"),sQuery(id+"F0.wireOp",EDGE,"E1.2"),sQuery(id+"F0.wireOp",EDGE,"E1.3"),sQuery(id+"F0.wireOp",EDGE,"E1.4"),sQuery(id+"F0.wireOp",EDGE,"E1.5"),sQuery(id+"F0.wireOp",EDGE,"E2.1.1"),sQuery(id+"F0.wireOp",EDGE,"E2.1.2"),sQuery(id+"F0.wireOp",EDGE,"E2.1.3"),sQuery(id+"F0.wireOp",EDGE,"E2.1.4"),sQuery(id+"F0.wireOp",EDGE,"E2.1.5"),sQuery(id+"F0.wireOp",EDGE,"E2.1.6"),sQuery(id+"F0.wireOp",EDGE,"E2.2.1"),sQuery(id+"F0.wireOp",EDGE,"E2.2.2"),sQuery(id+"F0.wireOp",EDGE,"E2.2.3"),sQuery(id+"F0.wireOp",EDGE,"E2.2.4"),sQuery(id+"F0.wireOp",EDGE,"E2.2.5"),sQuery(id+"F0.wireOp",EDGE,"E2.2.6"),subQ1,sQuery(id+"F0.wireOp",EDGE,"E4"),sQuery(id+"F0.wireOp",EDGE,"E5"),sQuery(id+"F0.wireOp",EDGE,"E6"),subQ0,sQuery(id+"F0.wireOp",EDGE,"E8"),sQuery(id+"F0.wireOp",EDGE,"E9.1.0"),sQuery(id+"F0.wireOp",EDGE,"E9.1.1"),sQuery(id+"F0.wireOp",EDGE,"E9.2.0"),sQuery(id+"F0.wireOp",EDGE,"E9.2.1"),sQuery(id+"F0.wireOp",EDGE,"E10.trimOffspring"),sQuery(id+"F0.wireOp",EDGE,"E11.trimOffspring")])],"isStart":true})],"blendedInto":[makeQuery(id+"F1.opExtrude","CAP_FACE",FACE,{"disambiguationData":[OSD([sQuery(id+"F0.wireOp",EDGE,"E0"),sQuery(id+"F0.wireOp",EDGE,"E1.0"),sQuery(id+"F0.wireOp",EDGE,"E1.1"),sQuery(id+"F0.wireOp",EDGE,"E1.2"),sQuery(id+"F0.wireOp",EDGE,"E1.3"),sQuery(id+"F0.wireOp",EDGE,"E1.4"),sQuery(id+"F0.wireOp",EDGE,"E1.5"),sQuery(id+"F0.wireOp",EDGE,"E2.1.1"),sQuery(id+"F0.wireOp",EDGE,"E2.1.2"),sQuery(id+"F0.wireOp",EDGE,"E2.1.3"),sQuery(id+"F0.wireOp",EDGE,"E2.1.4"),sQuery(id+"F0.wireOp",EDGE,"E2.1.5"),sQuery(id+"F0.wireOp",EDGE,"E2.1.6"),sQuery(id+"F0.wireOp",EDGE,"E2.2.1"),sQuery(id+"F0.wireOp",EDGE,"E2.2.2"),sQuery(id+"F0.wireOp",EDGE,"E2.2.3"),sQuery(id+"F0.wireOp",EDGE,"E2.2.4"),sQuery(id+"F0.wireOp",EDGE,"E2.2.5"),sQuery(id+"F0.wireOp",EDGE,"E2.2.6"),subQ1,sQuery(id+"F0.wireOp",EDGE,"E4"),sQuery(id+"F0.wireOp",EDGE,"E5"),sQuery(id+"F0.wireOp",EDGE,"E6"),subQ0,sQuery(id+"F0.wireOp",EDGE,"E8"),sQuery(id+"F0.wireOp",EDGE,"E9.1.0"),sQuery(id+"F0.wireOp",EDGE,"E9.1.1"),sQuery(id+"F0.wireOp",EDGE,"E9.2.0"),sQuery(id+"F0.wireOp",EDGE,"E9.2.1"),sQuery(id+"F0.wireOp",EDGE,"E10.trimOffspring"),sQuery(id+"F0.wireOp",EDGE,"E11.trimOffspring")])],"isStart":true})]});}
            var Q14;
            {var subQ0=sQuery(id+"F0.wireOp",EDGE,"E9.1.0");var subQ1=sQuery(id+"F0.wireOp",EDGE,"E3.0");Q14=makeQuery(id+"F2.opFillet","BLEND_EDGE",EDGE,{"blendedFrom":[makeQuery(id+"F1.opExtrude","SWEPT_EDGE",EDGE,{"disambiguationData":[OSD([subQ1,subQ0])]}),makeQuery(id+"F1.opExtrude","CAP_FACE",FACE,{"disambiguationData":[OSD([sQuery(id+"F0.wireOp",EDGE,"E0"),sQuery(id+"F0.wireOp",EDGE,"E1.0"),sQuery(id+"F0.wireOp",EDGE,"E1.1"),sQuery(id+"F0.wireOp",EDGE,"E1.2"),sQuery(id+"F0.wireOp",EDGE,"E1.3"),sQuery(id+"F0.wireOp",EDGE,"E1.4"),sQuery(id+"F0.wireOp",EDGE,"E1.5"),sQuery(id+"F0.wireOp",EDGE,"E2.1.1"),sQuery(id+"F0.wireOp",EDGE,"E2.1.2"),sQuery(id+"F0.wireOp",EDGE,"E2.1.3"),sQuery(id+"F0.wireOp",EDGE,"E2.1.4"),sQuery(id+"F0.wireOp",EDGE,"E2.1.5"),sQuery(id+"F0.wireOp",EDGE,"E2.1.6"),sQuery(id+"F0.wireOp",EDGE,"E2.2.1"),sQuery(id+"F0.wireOp",EDGE,"E2.2.2"),sQuery(id+"F0.wireOp",EDGE,"E2.2.3"),sQuery(id+"F0.wireOp",EDGE,"E2.2.4"),sQuery(id+"F0.wireOp",EDGE,"E2.2.5"),sQuery(id+"F0.wireOp",EDGE,"E2.2.6"),subQ1,sQuery(id+"F0.wireOp",EDGE,"E4"),sQuery(id+"F0.wireOp",EDGE,"E5"),sQuery(id+"F0.wireOp",EDGE,"E6"),sQuery(id+"F0.wireOp",EDGE,"E7"),sQuery(id+"F0.wireOp",EDGE,"E8"),subQ0,sQuery(id+"F0.wireOp",EDGE,"E9.1.1"),sQuery(id+"F0.wireOp",EDGE,"E9.2.0"),sQuery(id+"F0.wireOp",EDGE,"E9.2.1"),sQuery(id+"F0.wireOp",EDGE,"E10.trimOffspring"),sQuery(id+"F0.wireOp",EDGE,"E11.trimOffspring")])],"isStart":true})],"blendedInto":[makeQuery(id+"F1.opExtrude","CAP_FACE",FACE,{"disambiguationData":[OSD([sQuery(id+"F0.wireOp",EDGE,"E0"),sQuery(id+"F0.wireOp",EDGE,"E1.0"),sQuery(id+"F0.wireOp",EDGE,"E1.1"),sQuery(id+"F0.wireOp",EDGE,"E1.2"),sQuery(id+"F0.wireOp",EDGE,"E1.3"),sQuery(id+"F0.wireOp",EDGE,"E1.4"),sQuery(id+"F0.wireOp",EDGE,"E1.5"),sQuery(id+"F0.wireOp",EDGE,"E2.1.1"),sQuery(id+"F0.wireOp",EDGE,"E2.1.2"),sQuery(id+"F0.wireOp",EDGE,"E2.1.3"),sQuery(id+"F0.wireOp",EDGE,"E2.1.4"),sQuery(id+"F0.wireOp",EDGE,"E2.1.5"),sQuery(id+"F0.wireOp",EDGE,"E2.1.6"),sQuery(id+"F0.wireOp",EDGE,"E2.2.1"),sQuery(id+"F0.wireOp",EDGE,"E2.2.2"),sQuery(id+"F0.wireOp",EDGE,"E2.2.3"),sQuery(id+"F0.wireOp",EDGE,"E2.2.4"),sQuery(id+"F0.wireOp",EDGE,"E2.2.5"),sQuery(id+"F0.wireOp",EDGE,"E2.2.6"),subQ1,sQuery(id+"F0.wireOp",EDGE,"E4"),sQuery(id+"F0.wireOp",EDGE,"E5"),sQuery(id+"F0.wireOp",EDGE,"E6"),sQuery(id+"F0.wireOp",EDGE,"E7"),sQuery(id+"F0.wireOp",EDGE,"E8"),subQ0,sQuery(id+"F0.wireOp",EDGE,"E9.1.1"),sQuery(id+"F0.wireOp",EDGE,"E9.2.0"),sQuery(id+"F0.wireOp",EDGE,"E9.2.1"),sQuery(id+"F0.wireOp",EDGE,"E10.trimOffspring"),sQuery(id+"F0.wireOp",EDGE,"E11.trimOffspring")])],"isStart":true})]});}
            var Q15;
            Q15=makeQuery(id+"F1.opExtrude","CAP_EDGE",EDGE,{"disambiguationData":[OSD([sQuery(id+"F0.wireOp",EDGE,"E6")])],"isStart":true});
            var Q16;
            {var subQ0=sQuery(id+"F0.wireOp",EDGE,"E10.trimOffspring");var subQ1=sQuery(id+"F0.wireOp",EDGE,"E9.1.1");Q16=makeQuery(id+"F2.opFillet","BLEND_EDGE",EDGE,{"blendedFrom":[makeQuery(id+"F1.opExtrude","SWEPT_EDGE",EDGE,{"disambiguationData":[OSD([subQ1,subQ0])]}),makeQuery(id+"F1.opExtrude","CAP_FACE",FACE,{"disambiguationData":[OSD([sQuery(id+"F0.wireOp",EDGE,"E0"),sQuery(id+"F0.wireOp",EDGE,"E1.0"),sQuery(id+"F0.wireOp",EDGE,"E1.1"),sQuery(id+"F0.wireOp",EDGE,"E1.2"),sQuery(id+"F0.wireOp",EDGE,"E1.3"),sQuery(id+"F0.wireOp",EDGE,"E1.4"),sQuery(id+"F0.wireOp",EDGE,"E1.5"),sQuery(id+"F0.wireOp",EDGE,"E2.1.1"),sQuery(id+"F0.wireOp",EDGE,"E2.1.2"),sQuery(id+"F0.wireOp",EDGE,"E2.1.3"),sQuery(id+"F0.wireOp",EDGE,"E2.1.4"),sQuery(id+"F0.wireOp",EDGE,"E2.1.5"),sQuery(id+"F0.wireOp",EDGE,"E2.1.6"),sQuery(id+"F0.wireOp",EDGE,"E2.2.1"),sQuery(id+"F0.wireOp",EDGE,"E2.2.2"),sQuery(id+"F0.wireOp",EDGE,"E2.2.3"),sQuery(id+"F0.wireOp",EDGE,"E2.2.4"),sQuery(id+"F0.wireOp",EDGE,"E2.2.5"),sQuery(id+"F0.wireOp",EDGE,"E2.2.6"),sQuery(id+"F0.wireOp",EDGE,"E3.0"),sQuery(id+"F0.wireOp",EDGE,"E4"),sQuery(id+"F0.wireOp",EDGE,"E5"),sQuery(id+"F0.wireOp",EDGE,"E6"),sQuery(id+"F0.wireOp",EDGE,"E7"),sQuery(id+"F0.wireOp",EDGE,"E8"),sQuery(id+"F0.wireOp",EDGE,"E9.1.0"),subQ1,sQuery(id+"F0.wireOp",EDGE,"E9.2.0"),sQuery(id+"F0.wireOp",EDGE,"E9.2.1"),subQ0,sQuery(id+"F0.wireOp",EDGE,"E11.trimOffspring")])],"isStart":true})],"blendedInto":[makeQuery(id+"F1.opExtrude","CAP_FACE",FACE,{"disambiguationData":[OSD([sQuery(id+"F0.wireOp",EDGE,"E0"),sQuery(id+"F0.wireOp",EDGE,"E1.0"),sQuery(id+"F0.wireOp",EDGE,"E1.1"),sQuery(id+"F0.wireOp",EDGE,"E1.2"),sQuery(id+"F0.wireOp",EDGE,"E1.3"),sQuery(id+"F0.wireOp",EDGE,"E1.4"),sQuery(id+"F0.wireOp",EDGE,"E1.5"),sQuery(id+"F0.wireOp",EDGE,"E2.1.1"),sQuery(id+"F0.wireOp",EDGE,"E2.1.2"),sQuery(id+"F0.wireOp",EDGE,"E2.1.3"),sQuery(id+"F0.wireOp",EDGE,"E2.1.4"),sQuery(id+"F0.wireOp",EDGE,"E2.1.5"),sQuery(id+"F0.wireOp",EDGE,"E2.1.6"),sQuery(id+"F0.wireOp",EDGE,"E2.2.1"),sQuery(id+"F0.wireOp",EDGE,"E2.2.2"),sQuery(id+"F0.wireOp",EDGE,"E2.2.3"),sQuery(id+"F0.wireOp",EDGE,"E2.2.4"),sQuery(id+"F0.wireOp",EDGE,"E2.2.5"),sQuery(id+"F0.wireOp",EDGE,"E2.2.6"),sQuery(id+"F0.wireOp",EDGE,"E3.0"),sQuery(id+"F0.wireOp",EDGE,"E4"),sQuery(id+"F0.wireOp",EDGE,"E5"),sQuery(id+"F0.wireOp",EDGE,"E6"),sQuery(id+"F0.wireOp",EDGE,"E7"),sQuery(id+"F0.wireOp",EDGE,"E8"),sQuery(id+"F0.wireOp",EDGE,"E9.1.0"),subQ1,sQuery(id+"F0.wireOp",EDGE,"E9.2.0"),sQuery(id+"F0.wireOp",EDGE,"E9.2.1"),subQ0,sQuery(id+"F0.wireOp",EDGE,"E11.trimOffspring")])],"isStart":true})]});}
            fillet(context, id + "F3", {"entities" : qUnion([Q0, Q1, Q2, Q3, Q4, Q5, Q6, Q7, Q8, Q9, Q10, Q11, Q12, Q13, Q14, Q15, Q16]), "radius" : 1.5 * mm, "tangentPropagation" : true, "allowEdgeOverflow" : false});
        }
    });
